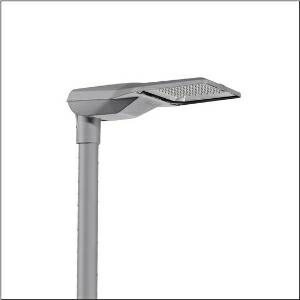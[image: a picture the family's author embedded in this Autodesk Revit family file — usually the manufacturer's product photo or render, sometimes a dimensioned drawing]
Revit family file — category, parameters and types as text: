
# Revit family: streetlight_sl_21_iq_midi___st0_5a_5xe3b31d08nb_970f
name_source: partatom
category: Lighting Fixtures
units: mm (PartAtom-declared; Revit-internal decimal feet)

## family parameters
Cut with Voids When Loaded = No
Host = Face
Light Source = No
Part Type = Normal
Room Calculation Point = No
Round Connector Dimension = Use Diameter
Shared = No

## types (1)
- --- (1 x LED, 23230 lm, 155.5 W, 3000K)
    Apparent Load = 155 VA
    CIE Flux Codes = 43 76 97 100 100
    Color Rendering = 70
    Color Temperature = 3000K
    Default Elevation = 1800 mm
    Description = Streetlight SL 21 iQ midi, mast luminaire, primary light control with lens, of PMMA, primary optical cover: cover, of toughened safety glass, transparent, light distribution: ST0.5a, light emission: direct distribution, primary light characteristic: asymmetric, installation type: post-top, side-entry, LED, High Power LED, rated luminous flux: 23.230lm, luminous efficacy: 149lm/W, light colour: 730, colour temperature: 3000K, control gear: iQ-Comfort, control: Auto-Match, Temp-Guard, Lumen-Switch, Night-Set, Smart-Wire, Light-Fading, Desk-Remote (wireless, voltage-free reading and setting of iQ features in the workshop via application-optimized NFC function/RFID function), optimised constant luminous flux control (CLO 2.0), pre-setting: linear dimming characteristic, mains connection: 230..240V, AC, 50/60Hz, start of lifetime: 156W, end of service life: 162W, reduction: 69W, luminaire housing, of diecast aluminium, powder-coated, Siteco® metallic grey (DB 702S), corrosivity category C5 mid according to DIN EN ISO 12944, please order mast flange separately, inclination adjustable: 0°, 5°, 10°, 15°, sealing non-destructively replaceable, multi-level sealing system, length: 644mm, width: 335mm, height: 110mm, mast flange for spigot size: 42mm (side-entry): 5XC10008XM4, 60/48mm (side-entry/post-top): 5XC10108XM2, 76/60mm (side-entry/post-top): 5XC10108XM1, mounting height: 4..8m, protection rating (complete): IP66, insulation class (complete): insulation class II (safety insulation), certification: CE, ENEC, ENEC+, VDE, impact resistance: IK10, permissible operating ambient temperature for outdoor applications: -40..+50°C, standard-compliant lighting for roads and squares, packaging unit: 1 piece

Light Distribution: ST0.5a
    Height = 111 mm
    Lamp = 1 x LED
    Lamp Light Flux = 23230 lm
    Lamp Power = 155.5 W
    Lamp count = 1
    Length = 644 mm
    Luminous efficacy = 149 lm/W
    Manufacturer = Siteco
    ModVariant = No
    Model = 5XE3B31D08NB
    Number of Poles = 1
    OnlyDefault = Yes
    Power Factor = 1
    Product Name = Streetlight SL 21 iQ midi | ST0.5a
    Product group = mast luminaire | pylon top
    ProductGroupID = 6100
    Protection Class = Protection class II
    Protection Degree = IP 66
    RLX_Detail_Level = 1
    RLX_Emergency_Light_Flux = 0 lm
    RLX_Emergency_Type = 0
    RLX_Emergency_Type_DB = No
    RlxData = <blob elided: 38389 chars, md5=1fcda595>
    Socket = socket
    Standby Power = 0 W
    System Light Flux = 23230 lm
    System Power = 155 W
    Type Comments = factory setting: luminous flux: 100 % | dim-lin: 254 | 823 mA
    Type Image = l_1004298.jpg
    URL = http://relux.com
    VarID = @adj_193051
    Voltage = 0 V
    Weight = 0.00 kg
    Width = 336 mm

## geometry (parser evidence)
native form markers: Blend x4, Sweep x7
no freeform markers — native parametric forms only
